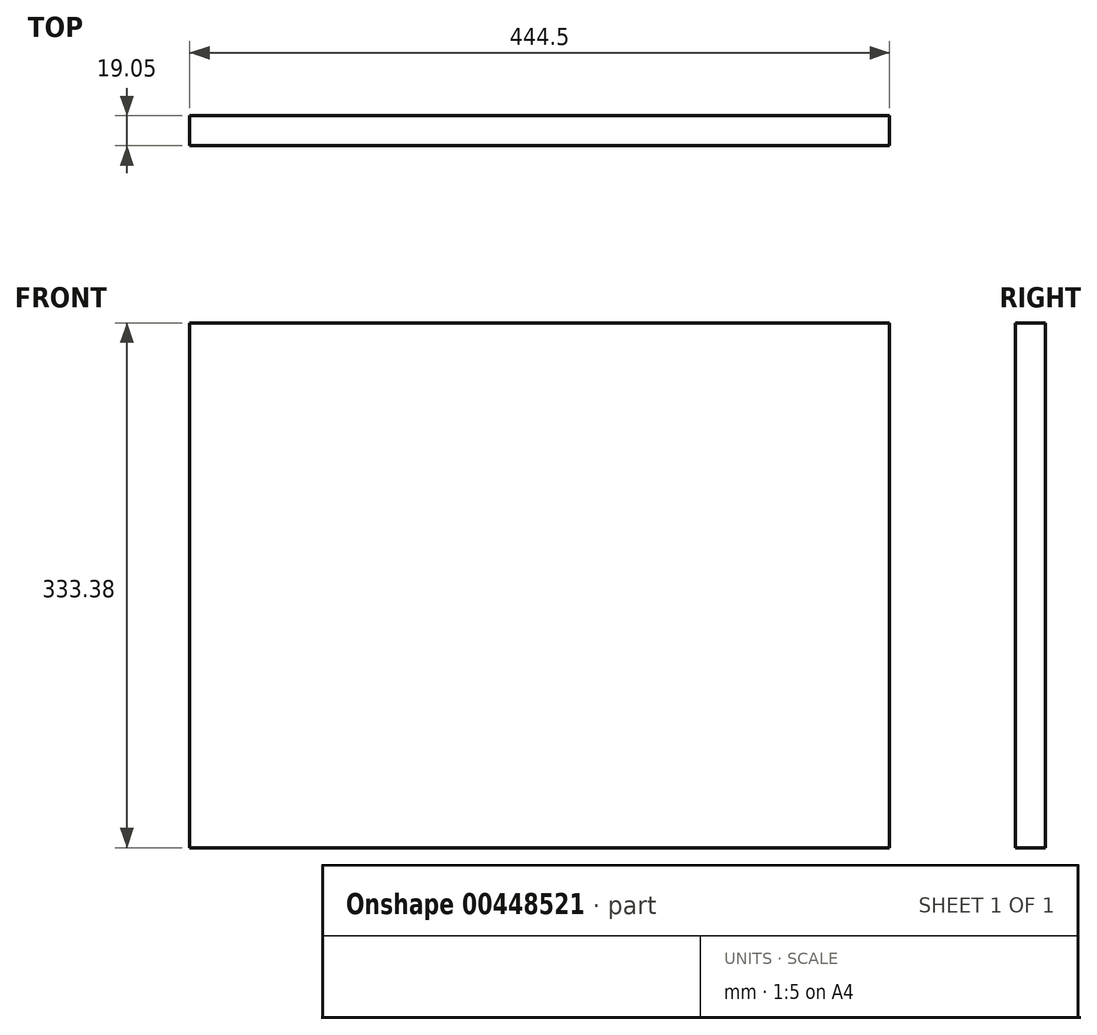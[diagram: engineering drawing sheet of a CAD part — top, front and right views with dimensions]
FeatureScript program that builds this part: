
annotation { "Feature Type Name" : "Feature", "Feature Type Description" : "" }
export const myFeature = defineFeature(function(context is Context, id is Id, definition is map)
    precondition{}
    {
        {
            var Q0;
            Q0=qCreatedBy(makeId("Front.planeOp"),FACE);
            var sketch = newSketch(context, id + "F0", { "sketchPlane" : qUnion([Q0])});
            skLineSegment(sketch, "E0.bottom", {"start": v(0, 0) * mm, "end": v(444.5, 0) * mm});
            skLineSegment(sketch, "E0.top", {"start": v(0, 333.38) * mm, "end": v(444.5, 333.38) * mm});
            skLineSegment(sketch, "E0.left", {"start": v(0, 0) * mm, "end": v(0, 333.38) * mm});
            skLineSegment(sketch, "E0.right", {"start": v(444.5, 0) * mm, "end": v(444.5, 333.38) * mm});
            skSolve(sketch);
        }
        {
            var Q0;
            Q0=makeQuery(id+"F0.imprint","IMPRINT",FACE,{"disambiguationData":[TD([[makeQuery(id+"F0.imprint","IMPRINT",EDGE,{"derivedFrom":sQuery(id+"F0.wireOp",EDGE,"E0.bottom")}),1.0]])]});
            extrude(context, id + "F1", {"entities" : qUnion([Q0]), "depth" : 19.05 * mm, "offsetDistance" : 25.4 * mm});
        }
    });
